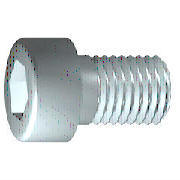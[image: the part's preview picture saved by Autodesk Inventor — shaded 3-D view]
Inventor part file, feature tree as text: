
AUTODESK INVENTOR PART (.ipt)
format: ipt  version: 2024.1 (Build 281209000, 209)  size: 192,512 bytes
history: native  units: mm (DEFAULTED — no unit token found)
features: extrude x1, plane x1, fillet x1
ambient origin geometry x7: Origin, YZ Plane, XY Plane, X Axis, Y Axis, Z Axis, Center Point
bodies: Solid1 (feature_tree), Body (feature_tree)
feature tree (3):
  extrude  "Slot"  Depth=8.75mm
  plane  "Work Plane1"
  fillet  "Fillet2"  Radius=0.306825mm
